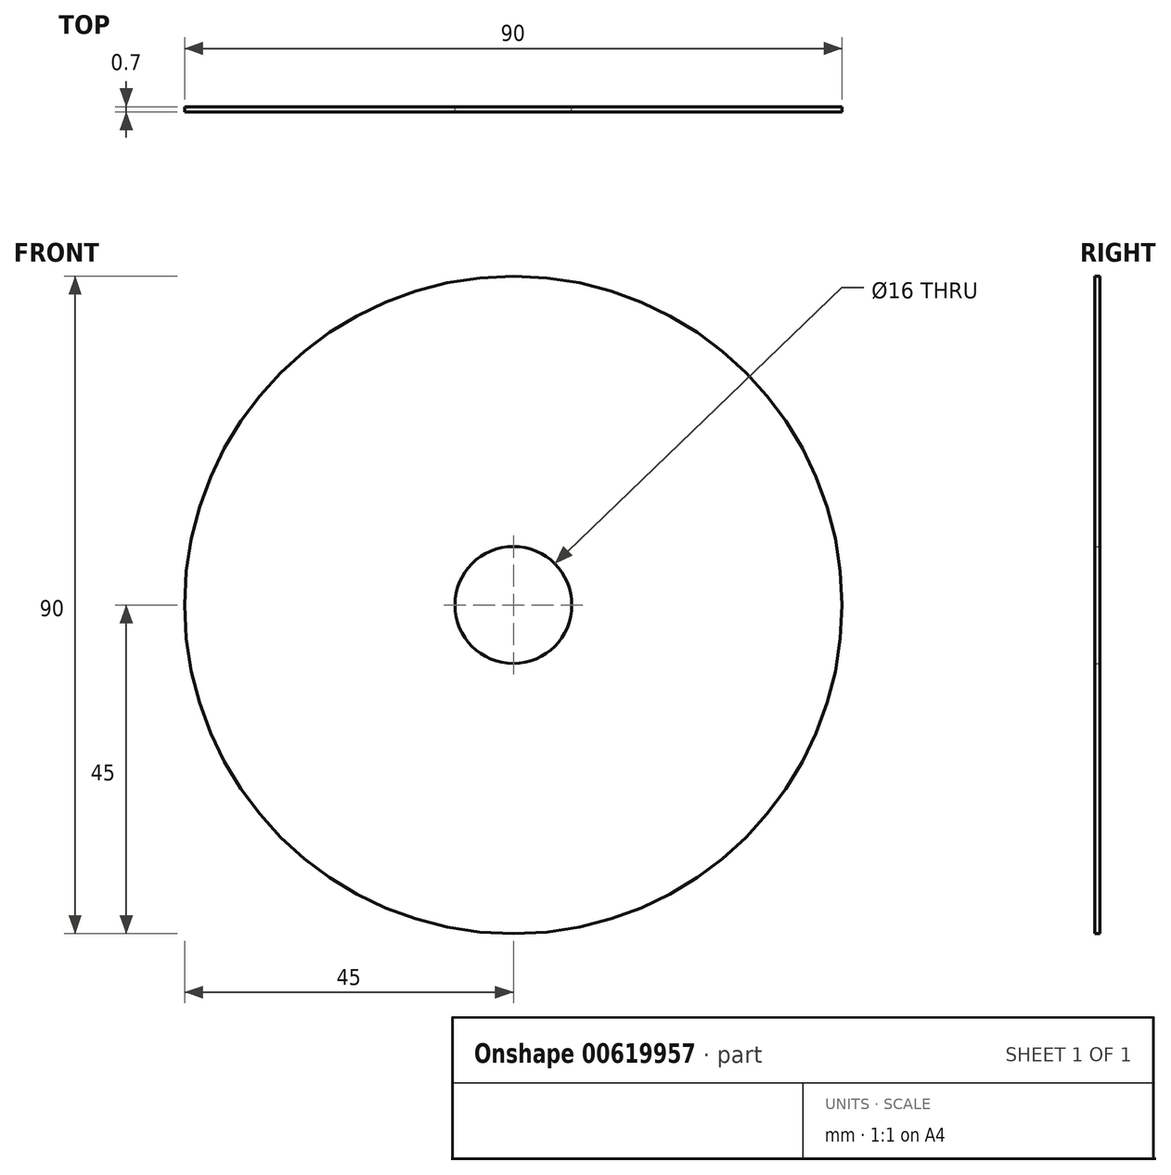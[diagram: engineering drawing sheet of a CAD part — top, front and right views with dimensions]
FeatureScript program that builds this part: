
annotation { "Feature Type Name" : "Feature", "Feature Type Description" : "" }
export const myFeature = defineFeature(function(context is Context, id is Id, definition is map)
    precondition{}
    {
        {
            var Q0;
            Q0=qCreatedBy(makeId("Front.planeOp"),FACE);
            var sketch = newSketch(context, id + "F0", { "sketchPlane" : qUnion([Q0])});
            skPoint(sketch, "E0", {"position": v(0, 0) * mm});
            skCircle(sketch, "E1", {"center": v(0, 0) * mm, "radius": 45 * mm});
            skCircle(sketch, "E2", {"center": v(0, 0) * mm, "radius": 8 * mm});
            skSolve(sketch);
        }
        {
            var Q0;
            Q0=makeQuery(id+"F0.imprint","IMPRINT",FACE,{"disambiguationData":[TD([[makeQuery(id+"F0.imprint","IMPRINT",EDGE,{"derivedFrom":sQuery(id+"F0.wireOp",EDGE,"E1")}),1.0]])]});
            extrude(context, id + "F1", {"entities" : qUnion([Q0]), "depth" : 0.7 * mm, "offsetDistance" : 25 * mm});
        }
    });
